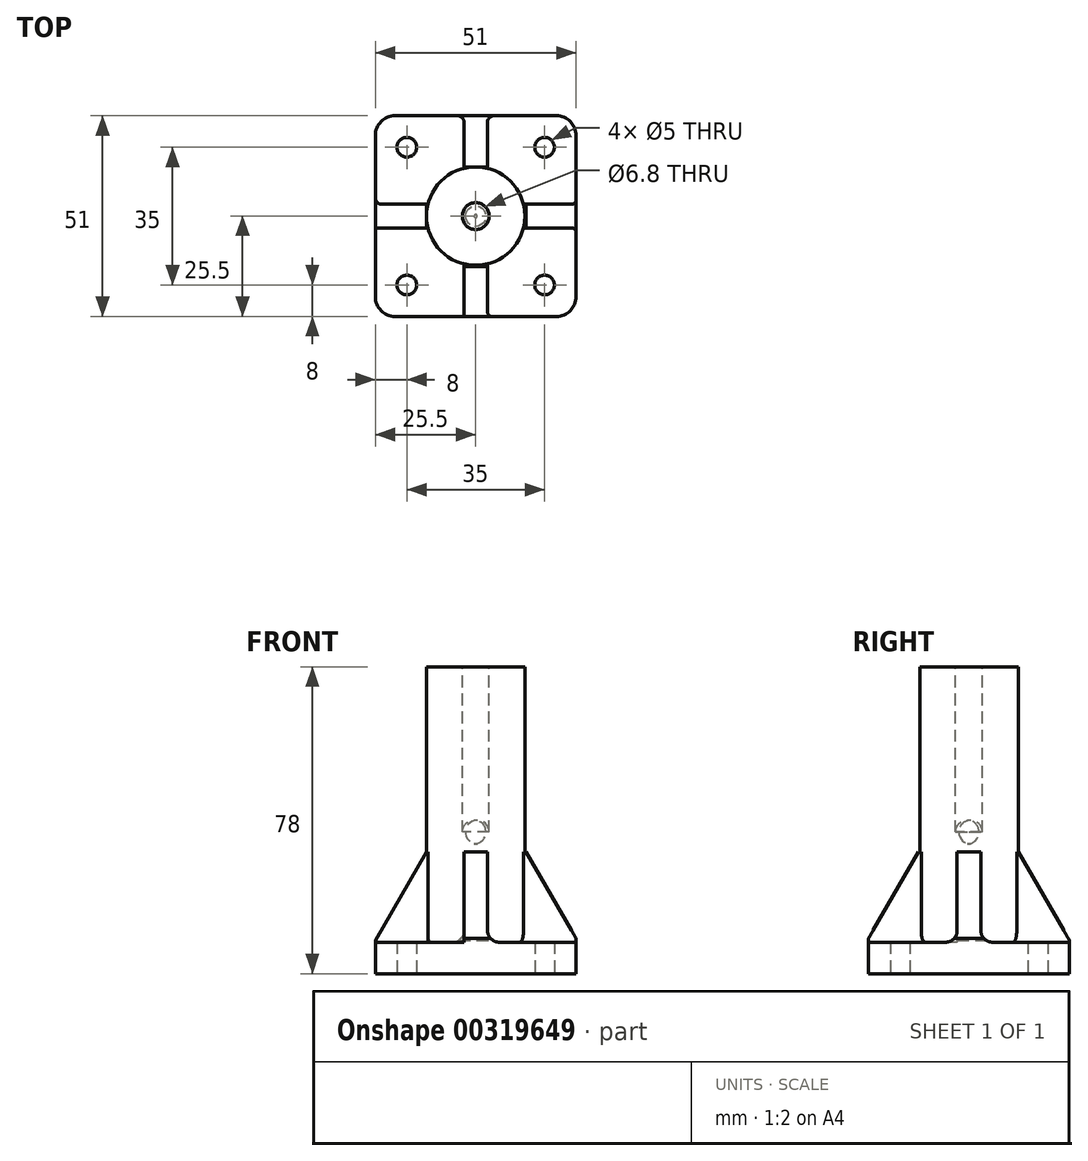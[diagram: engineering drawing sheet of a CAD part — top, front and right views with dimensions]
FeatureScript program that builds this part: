
annotation { "Feature Type Name" : "Feature", "Feature Type Description" : "" }
export const myFeature = defineFeature(function(context is Context, id is Id, definition is map)
    precondition{}
    {
        {
            var Q0;
            Q0=qCreatedBy(makeId("Top.planeOp"),FACE);
            var sketch = newSketch(context, id + "F0", { "sketchPlane" : qUnion([Q0])});
            skLineSegment(sketch, "E0.bottom", {"start": v(17.5, 17.5) * mm, "end": v(-17.5, 17.5) * mm, "construction": true});
            skLineSegment(sketch, "E0.top", {"start": v(17.5, -17.5) * mm, "end": v(-17.5, -17.5) * mm, "construction": true});
            skLineSegment(sketch, "E0.left", {"start": v(17.5, 17.5) * mm, "end": v(17.5, -17.5) * mm, "construction": true});
            skLineSegment(sketch, "E0.right", {"start": v(-17.5, 17.5) * mm, "end": v(-17.5, -17.5) * mm, "construction": true});
            skPoint(sketch, "E0.middle", {"position": v(0, 0) * mm});
            skCircle(sketch, "E1", {"center": v(-17.5, 17.5) * mm, "radius": 2.5 * mm});
            skCircle(sketch, "E2", {"center": v(17.5, 17.5) * mm, "radius": 2.5 * mm});
            skCircle(sketch, "E3", {"center": v(17.5, -17.5) * mm, "radius": 2.5 * mm});
            skCircle(sketch, "E4", {"center": v(-17.5, -17.5) * mm, "radius": 2.5 * mm});
            skLineSegment(sketch, "E5.0", {"start": v(25.5, 25.5) * mm, "end": v(-25.5, 25.5) * mm});
            skLineSegment(sketch, "E5.1", {"start": v(25.5, 25.5) * mm, "end": v(25.5, -25.5) * mm});
            skLineSegment(sketch, "E5.2", {"start": v(25.5, -25.5) * mm, "end": v(-25.5, -25.5) * mm});
            skLineSegment(sketch, "E5.3", {"start": v(-25.5, 25.5) * mm, "end": v(-25.5, -25.5) * mm});
            skSolve(sketch);
        }
        {
            var Q0;
            Q0=makeQuery(id+"F0.imprint","IMPRINT",FACE,{"disambiguationData":[TD([[makeQuery(id+"F0.imprint","IMPRINT",EDGE,{"derivedFrom":sQuery(id+"F0.wireOp",EDGE,"E1")}),-1.0]])]});
            extrude(context, id + "F1", {"entities" : qUnion([Q0]), "depth" : 8 * mm});
        }
        {
            var Q0;
            Q0=makeQuery(id+"F1.opExtrude","CAP_FACE",FACE,{"disambiguationData":[OSD([sQuery(id+"F0.wireOp",EDGE,"E1"),sQuery(id+"F0.wireOp",EDGE,"E2"),sQuery(id+"F0.wireOp",EDGE,"E3"),sQuery(id+"F0.wireOp",EDGE,"E4"),sQuery(id+"F0.wireOp",EDGE,"E5.0"),sQuery(id+"F0.wireOp",EDGE,"E5.1"),sQuery(id+"F0.wireOp",EDGE,"E5.2"),sQuery(id+"F0.wireOp",EDGE,"E5.3")])],"isStart":false});
            var sketch = newSketch(context, id + "F2", { "sketchPlane" : qUnion([Q0])});
            skPoint(sketch, "E6.0", {"position": v(0, 0) * mm});
            skCircle(sketch, "E7", {"center": v(0, 0) * mm, "radius": 12.5 * mm});
            skLineSegment(sketch, "E8", {"start": v(0, 25.5) * mm, "end": v(0, -25.5) * mm, "construction": true});
            skLineSegment(sketch, "E9", {"start": v(-25.5, 0) * mm, "end": v(25.5, 0) * mm, "construction": true});
            skLineSegment(sketch, "E10.0", {"start": v(-3, 25.5) * mm, "end": v(-3, 12.13) * mm});
            skLineSegment(sketch, "E11.0", {"start": v(3, 25.5) * mm, "end": v(3, 12.13) * mm});
            skLineSegment(sketch, "E12.0", {"start": v(-25.5, -3) * mm, "end": v(-12.13, -3) * mm});
            skLineSegment(sketch, "E13.0", {"start": v(-25.5, 3) * mm, "end": v(-12.13, 3) * mm});
            skLineSegment(sketch, "E14.trimOffspring", {"start": v(3, -12.13) * mm, "end": v(3, -25.5) * mm});
            skLineSegment(sketch, "E15.trimOffspring", {"start": v(12.13, 3) * mm, "end": v(25.5, 3) * mm});
            skLineSegment(sketch, "E16.trimOffspring", {"start": v(12.13, -3) * mm, "end": v(25.5, -3) * mm});
            skLineSegment(sketch, "E17.trimOffspring", {"start": v(-3, -12.13) * mm, "end": v(-3, -25.5) * mm});
            skLineSegment(sketch, "E18", {"start": v(-3, 25.5) * mm, "end": v(3, 25.5) * mm});
            skLineSegment(sketch, "E19", {"start": v(25.5, 3) * mm, "end": v(25.5, -3) * mm});
            skLineSegment(sketch, "E20", {"start": v(-25.5, 3) * mm, "end": v(-25.5, -3) * mm});
            skLineSegment(sketch, "E21", {"start": v(-3, -25.5) * mm, "end": v(3, -25.5) * mm});
            skSolve(sketch);
        }
        {
            var Q0;
            Q0=makeQuery(id+"F2.imprint","IMPRINT",FACE,{"disambiguationData":[TD([[makeQuery(id+"F2.imprint","IMPRINT",EDGE,{"derivedFrom":sQuery(id+"F2.wireOp",EDGE,"E7")}),1.0]])]});
            extrude(context, id + "F3", {"entities" : qUnion([Q0]), "operationType" : NewBodyOperationType.ADD, "depth" : 70 * mm});
        }
        {
            var Q0;
            {var subQ0=sQuery(id+"F2.wireOp",EDGE,"E12.0");Q0=makeQuery(id+"F2.imprint","IMPRINT",FACE,{"disambiguationData":[TD([[makeQuery(id+"F2.imprint","IMPRINT",EDGE,{"derivedFrom":subQ0}),1.0]])]});}
            var Q1;
            {var subQ0=sQuery(id+"F2.wireOp",EDGE,"E14.trimOffspring");Q1=makeQuery(id+"F2.imprint","IMPRINT",FACE,{"disambiguationData":[TD([[makeQuery(id+"F2.imprint","IMPRINT",EDGE,{"derivedFrom":subQ0}),-1.0]])]});}
            var Q2;
            {var subQ0=sQuery(id+"F2.wireOp",EDGE,"E15.trimOffspring");Q2=makeQuery(id+"F2.imprint","IMPRINT",FACE,{"disambiguationData":[TD([[makeQuery(id+"F2.imprint","IMPRINT",EDGE,{"derivedFrom":subQ0}),-1.0]])]});}
            var Q3;
            {var subQ0=sQuery(id+"F2.wireOp",EDGE,"E10.0");Q3=makeQuery(id+"F2.imprint","IMPRINT",FACE,{"disambiguationData":[TD([[makeQuery(id+"F2.imprint","IMPRINT",EDGE,{"derivedFrom":subQ0}),1.0]])]});}
            extrude(context, id + "F4", {"entities" : qUnion([Q0, Q1, Q2, Q3]), "operationType" : NewBodyOperationType.ADD, "depth" : 23 * mm});
        }
        {
            var Q0;
            Q0=makeQuery(id+"F4.opExtrude","CAP_EDGE",EDGE,{"disambiguationData":[OSD([sQuery(id+"F2.wireOp",EDGE,"E20")])],"isStart":false});
            var Q1;
            Q1=makeQuery(id+"F4.opExtrude","CAP_EDGE",EDGE,{"disambiguationData":[OSD([sQuery(id+"F2.wireOp",EDGE,"E18")])],"isStart":false});
            chamfer(context, id + "F5", {"entities" : qUnion([Q0, Q1]), "chamferType" : ChamferType.OFFSET_ANGLE, "width" : 13 * mm, "oppositeDirection" : false, "angle" : 60 * degree});
        }
        {
            var Q0;
            Q0=makeQuery(id+"F4.opExtrude","CAP_EDGE",EDGE,{"disambiguationData":[OSD([sQuery(id+"F2.wireOp",EDGE,"E19")])],"isStart":false});
            var Q1;
            Q1=makeQuery(id+"F4.opExtrude","CAP_EDGE",EDGE,{"disambiguationData":[OSD([sQuery(id+"F2.wireOp",EDGE,"E21")])],"isStart":false});
            chamfer(context, id + "F6", {"entities" : qUnion([Q0, Q1]), "chamferType" : ChamferType.OFFSET_ANGLE, "width" : 22 * mm, "oppositeDirection" : false, "angle" : 30 * degree, "tangentPropagation" : true});
        }
        {
            var Q0;
            Q0=makeQuery(id+"F3.opExtrude","CAP_FACE",FACE,{"disambiguationData":[OSD([sQuery(id+"F2.wireOp",EDGE,"E7")])],"isStart":false});
            var sketch = newSketch(context, id + "F7", { "sketchPlane" : qUnion([Q0])});
            skPoint(sketch, "E22.0", {"position": v(0, 0) * mm});
            skCircle(sketch, "E23", {"center": v(0, 0) * mm, "radius": 3.4 * mm});
            skSolve(sketch);
        }
        {
            var Q0;
            Q0=makeQuery(id+"F7.imprint","IMPRINT",FACE,{"disambiguationData":[TD([[makeQuery(id+"F7.imprint","IMPRINT",EDGE,{"derivedFrom":sQuery(id+"F7.wireOp",EDGE,"E23")}),1.0]])]});
            extrude(context, id + "F8", {"entities" : qUnion([Q0]), "operationType" : NewBodyOperationType.REMOVE, "oppositeDirection" : true, "depth" : 45 * mm});
        }
        {
            var Q0;
            {var subQ0=sQuery(id+"F2.wireOp",EDGE,"E7");Q0=makeQuery(id+"F4.boolean.opBoolean","SPLIT",EDGE,{"disambiguationData":[TD([makeQuery(id+"F4.opExtrude","SWEPT_FACE",FACE,{"disambiguationData":[OSD([sQuery(id+"F2.wireOp",EDGE,"E10.0")])]})])],"derivedFrom":makeQuery(id+"F3.opExtrude","CAP_EDGE",EDGE,{"disambiguationData":[OSD([subQ0])],"isStart":true})});}
            var Q1;
            Q1=makeQuery(id+"F4.opExtrude","CAP_EDGE",EDGE,{"disambiguationData":[OSD([sQuery(id+"F2.wireOp",EDGE,"E13.0")])],"isStart":true});
            var Q2;
            Q2=makeQuery(id+"F4.opExtrude","CAP_EDGE",EDGE,{"disambiguationData":[OSD([sQuery(id+"F2.wireOp",EDGE,"E10.0")])],"isStart":true});
            var Q3;
            Q3=makeQuery(id+"F4.opExtrude","CAP_EDGE",EDGE,{"disambiguationData":[OSD([sQuery(id+"F2.wireOp",EDGE,"E11.0")])],"isStart":true});
            var Q4;
            Q4=makeQuery(id+"F4.opExtrude","SWEPT_EDGE",EDGE,{"disambiguationData":[OSD([sQuery(id+"F2.wireOp",EDGE,"E7"),sQuery(id+"F2.wireOp",EDGE,"E11.0")])]});
            var Q5;
            Q5=makeQuery(id+"F4.opExtrude","SWEPT_EDGE",EDGE,{"disambiguationData":[OSD([sQuery(id+"F2.wireOp",EDGE,"E7"),sQuery(id+"F2.wireOp",EDGE,"E15.trimOffspring")])]});
            var Q6;
            Q6=makeQuery(id+"F4.opExtrude","CAP_EDGE",EDGE,{"disambiguationData":[OSD([sQuery(id+"F2.wireOp",EDGE,"E15.trimOffspring")])],"isStart":true});
            var Q7;
            Q7=makeQuery(id+"F4.opExtrude","CAP_EDGE",EDGE,{"disambiguationData":[OSD([sQuery(id+"F2.wireOp",EDGE,"E16.trimOffspring")])],"isStart":true});
            var Q8;
            Q8=makeQuery(id+"F4.opExtrude","SWEPT_EDGE",EDGE,{"disambiguationData":[OSD([sQuery(id+"F2.wireOp",EDGE,"E7"),sQuery(id+"F2.wireOp",EDGE,"E16.trimOffspring")])]});
            var Q9;
            Q9=makeQuery(id+"F4.opExtrude","SWEPT_EDGE",EDGE,{"disambiguationData":[OSD([sQuery(id+"F2.wireOp",EDGE,"E7"),sQuery(id+"F2.wireOp",EDGE,"E14.trimOffspring")])]});
            var Q10;
            Q10=makeQuery(id+"F4.opExtrude","CAP_EDGE",EDGE,{"disambiguationData":[OSD([sQuery(id+"F2.wireOp",EDGE,"E14.trimOffspring")])],"isStart":true});
            var Q11;
            Q11=makeQuery(id+"F4.opExtrude","SWEPT_EDGE",EDGE,{"disambiguationData":[OSD([sQuery(id+"F2.wireOp",EDGE,"E7"),sQuery(id+"F2.wireOp",EDGE,"E17.trimOffspring")])]});
            var Q12;
            Q12=makeQuery(id+"F4.opExtrude","CAP_EDGE",EDGE,{"disambiguationData":[OSD([sQuery(id+"F2.wireOp",EDGE,"E17.trimOffspring")])],"isStart":true});
            var Q13;
            Q13=makeQuery(id+"F4.opExtrude","SWEPT_EDGE",EDGE,{"disambiguationData":[OSD([sQuery(id+"F2.wireOp",EDGE,"E7"),sQuery(id+"F2.wireOp",EDGE,"E12.0")])]});
            var Q14;
            Q14=makeQuery(id+"F4.opExtrude","CAP_EDGE",EDGE,{"disambiguationData":[OSD([sQuery(id+"F2.wireOp",EDGE,"E12.0")])],"isStart":true});
            var Q15;
            Q15=makeQuery(id+"F4.opExtrude","SWEPT_EDGE",EDGE,{"disambiguationData":[OSD([sQuery(id+"F2.wireOp",EDGE,"E7"),sQuery(id+"F2.wireOp",EDGE,"E10.0")])]});
            var Q16;
            Q16=makeQuery(id+"F8.boolean.opBoolean","COPY",EDGE,{"derivedFrom":makeQuery(id+"F8.opExtrude","CAP_EDGE",EDGE,{"disambiguationData":[OSD([sQuery(id+"F7.wireOp",EDGE,"E23")])],"isStart":false})});
            fillet(context, id + "F9", {"entities" : qUnion([Q0, Q1, Q2, Q3, Q4, Q5, Q6, Q7, Q8, Q9, Q10, Q11, Q12, Q13, Q14, Q15, Q16]), "radius" : 3 * mm, "tangentPropagation" : true, "allowEdgeOverflow" : false});
        }
        {
            var Q0;
            Q0=makeQuery(id+"F1.opExtrude","SWEPT_EDGE",EDGE,{"disambiguationData":[OSD([sQuery(id+"F0.wireOp",EDGE,"E5.0"),sQuery(id+"F0.wireOp",EDGE,"E5.1")])]});
            var Q1;
            Q1=makeQuery(id+"F1.opExtrude","SWEPT_EDGE",EDGE,{"disambiguationData":[OSD([sQuery(id+"F0.wireOp",EDGE,"E5.0"),sQuery(id+"F0.wireOp",EDGE,"E5.3")])]});
            var Q2;
            Q2=makeQuery(id+"F1.opExtrude","SWEPT_EDGE",EDGE,{"disambiguationData":[OSD([sQuery(id+"F0.wireOp",EDGE,"E5.2"),sQuery(id+"F0.wireOp",EDGE,"E5.3")])]});
            var Q3;
            Q3=makeQuery(id+"F1.opExtrude","SWEPT_EDGE",EDGE,{"disambiguationData":[OSD([sQuery(id+"F0.wireOp",EDGE,"E5.1"),sQuery(id+"F0.wireOp",EDGE,"E5.2")])]});
            fillet(context, id + "F10", {"entities" : qUnion([Q0, Q1, Q2, Q3]), "radius" : 5 * mm, "tangentPropagation" : true, "allowEdgeOverflow" : false});
        }
    });
